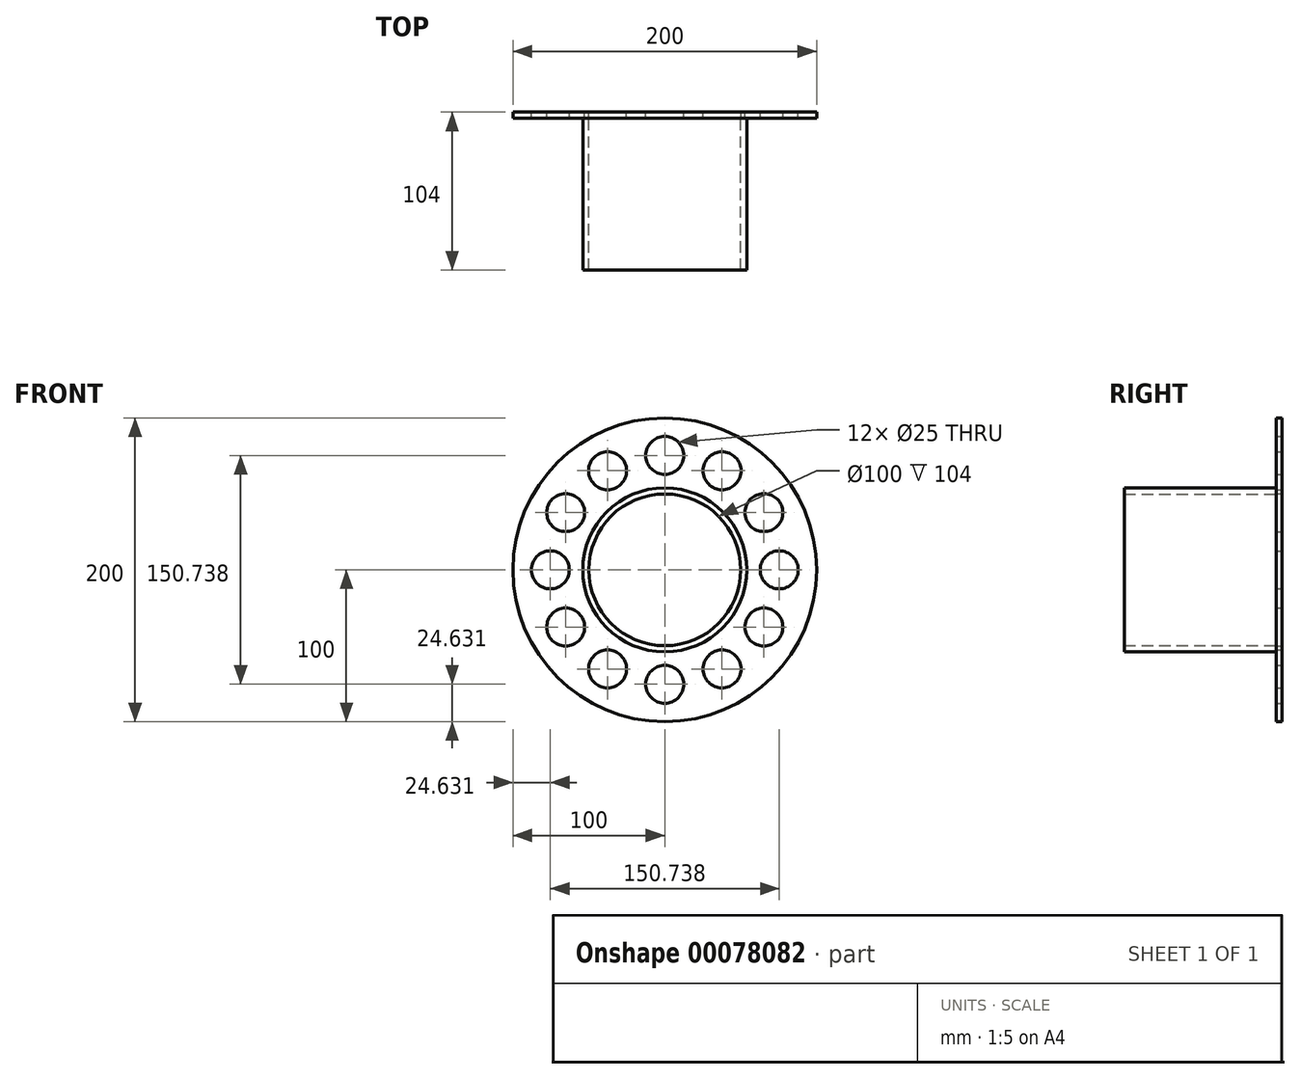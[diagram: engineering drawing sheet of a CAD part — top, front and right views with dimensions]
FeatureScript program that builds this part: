
annotation { "Feature Type Name" : "Feature", "Feature Type Description" : "" }
export const myFeature = defineFeature(function(context is Context, id is Id, definition is map)
    precondition{}
    {
        {
            var Q0;
            Q0=qCreatedBy(makeId("Front.planeOp"),FACE);
            var sketch = newSketch(context, id + "F0", { "sketchPlane" : qUnion([Q0])});
            skCircle(sketch, "E0", {"center": v(0, 0) * mm, "radius": 100 * mm});
            skCircle(sketch, "E1", {"center": v(0, 0) * mm, "radius": 50 * mm});
            skCircle(sketch, "E2", {"center": v(0, 75.37) * mm, "radius": 12.5 * mm});
            skCircle(sketch, "E3.1.0", {"center": v(-37.68, 65.27) * mm, "radius": 12.5 * mm});
            skCircle(sketch, "E3.2.0", {"center": v(-65.27, 37.68) * mm, "radius": 12.5 * mm});
            skCircle(sketch, "E3.3.0", {"center": v(-75.37, 0) * mm, "radius": 12.5 * mm});
            skCircle(sketch, "E3.4.0", {"center": v(-65.27, -37.68) * mm, "radius": 12.5 * mm});
            skCircle(sketch, "E3.5.0", {"center": v(-37.68, -65.27) * mm, "radius": 12.5 * mm});
            skCircle(sketch, "E3.6.0", {"center": v(0, -75.37) * mm, "radius": 12.5 * mm});
            skCircle(sketch, "E3.7.0", {"center": v(37.68, -65.27) * mm, "radius": 12.5 * mm});
            skCircle(sketch, "E3.8.0", {"center": v(65.27, -37.68) * mm, "radius": 12.5 * mm});
            skCircle(sketch, "E3.9.0", {"center": v(75.37, 0) * mm, "radius": 12.5 * mm});
            skCircle(sketch, "E3.10.0", {"center": v(65.27, 37.68) * mm, "radius": 12.5 * mm});
            skCircle(sketch, "E3.11.0", {"center": v(37.68, 65.27) * mm, "radius": 12.5 * mm});
            skSolve(sketch);
        }
        {
            var Q0;
            Q0=makeQuery(id+"F0.imprint","IMPRINT",FACE,{"disambiguationData":[TD([[makeQuery(id+"F0.imprint","IMPRINT",EDGE,{"derivedFrom":sQuery(id+"F0.wireOp",EDGE,"E0")}),1.0]])]});
            extrude(context, id + "F1", {"entities" : qUnion([Q0]), "depth" : 4 * mm});
        }
        {
            var Q0;
            Q0=makeQuery(id+"F1.opExtrude","CAP_FACE",FACE,{"disambiguationData":[OSD([sQuery(id+"F0.wireOp",EDGE,"E0"),sQuery(id+"F0.wireOp",EDGE,"E1"),sQuery(id+"F0.wireOp",EDGE,"E2"),sQuery(id+"F0.wireOp",EDGE,"E3.1.0"),sQuery(id+"F0.wireOp",EDGE,"E3.2.0"),sQuery(id+"F0.wireOp",EDGE,"E3.3.0"),sQuery(id+"F0.wireOp",EDGE,"E3.4.0"),sQuery(id+"F0.wireOp",EDGE,"E3.5.0"),sQuery(id+"F0.wireOp",EDGE,"E3.6.0"),sQuery(id+"F0.wireOp",EDGE,"E3.7.0"),sQuery(id+"F0.wireOp",EDGE,"E3.8.0"),sQuery(id+"F0.wireOp",EDGE,"E3.9.0"),sQuery(id+"F0.wireOp",EDGE,"E3.10.0"),sQuery(id+"F0.wireOp",EDGE,"E3.11.0")])],"isStart":false});
            var sketch = newSketch(context, id + "F2", { "sketchPlane" : qUnion([Q0])});
            skCircle(sketch, "E4", {"center": v(0, 0) * mm, "radius": 50 * mm});
            skCircle(sketch, "E5", {"center": v(0, 0) * mm, "radius": 54 * mm});
            skSolve(sketch);
        }
        {
            var Q0;
            Q0 = qSketchRegion(id + "F2", true);
            extrude(context, id + "F3", {"entities" : qUnion([Q0]), "operationType" : NewBodyOperationType.ADD, "depth" : 100 * mm});
        }
    });
